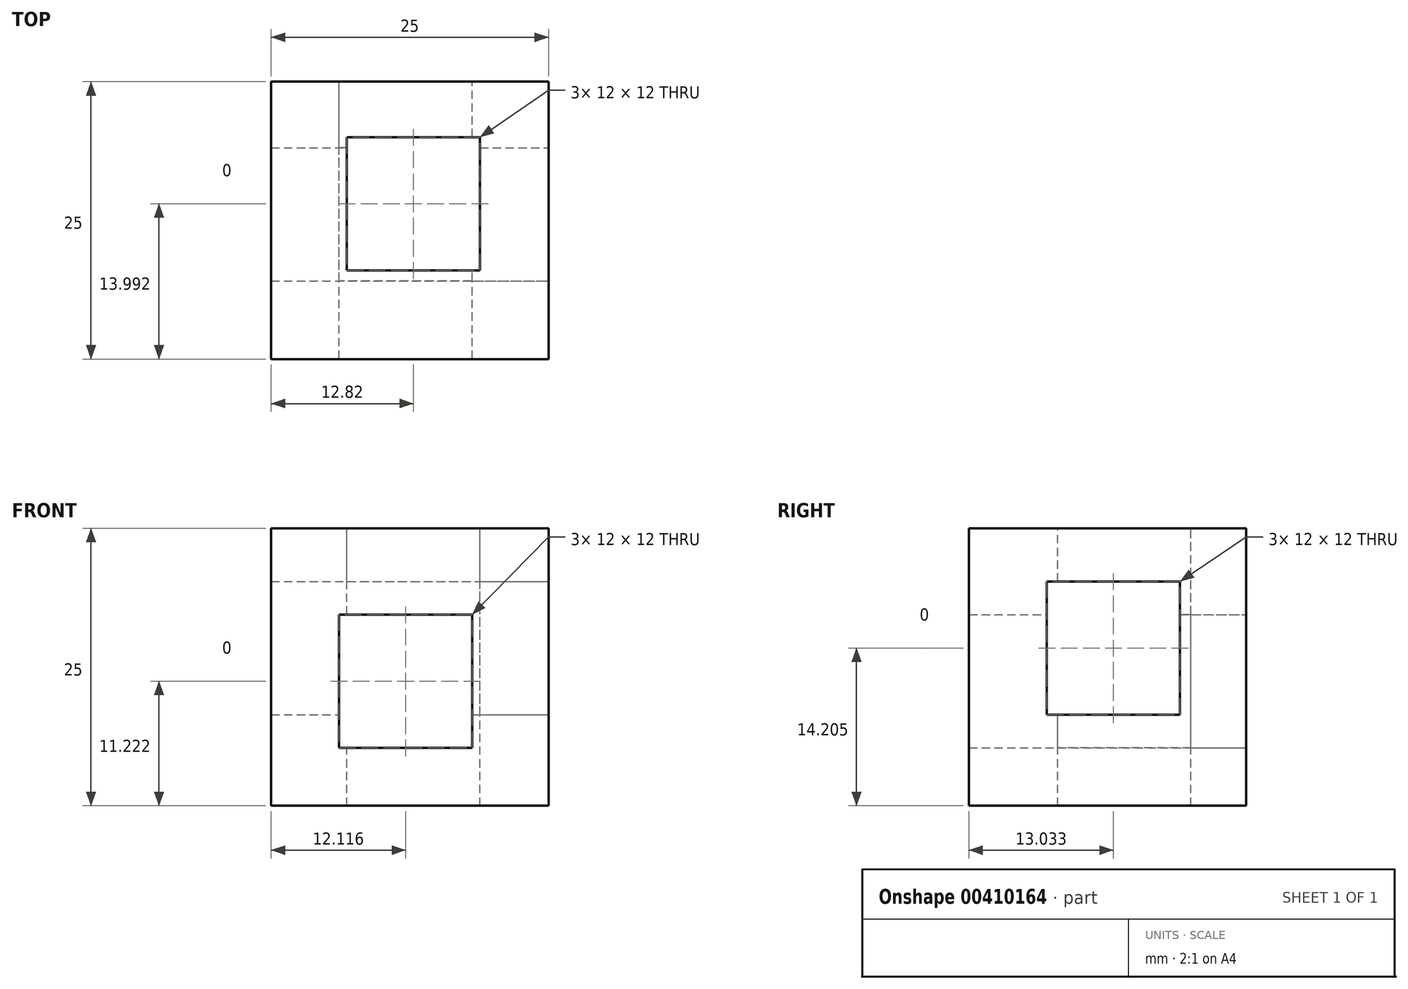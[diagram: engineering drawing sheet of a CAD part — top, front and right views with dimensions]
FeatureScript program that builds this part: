
annotation { "Feature Type Name" : "Feature", "Feature Type Description" : "" }
export const myFeature = defineFeature(function(context is Context, id is Id, definition is map)
    precondition{}
    {
        {
            var Q0;
            Q0=qCreatedBy(makeId("Top.planeOp"),FACE);
            var sketch = newSketch(context, id + "F0", { "sketchPlane" : qUnion([Q0])});
            skLineSegment(sketch, "E0.bottom", {"start": v(0, 0) * mm, "end": v(25, 0) * mm});
            skLineSegment(sketch, "E0.top", {"start": v(0, 25) * mm, "end": v(25, 25) * mm});
            skLineSegment(sketch, "E0.left", {"start": v(0, 0) * mm, "end": v(0, 25) * mm});
            skLineSegment(sketch, "E0.right", {"start": v(25, 0) * mm, "end": v(25, 25) * mm});
            skSolve(sketch);
        }
        {
            var Q0;
            Q0=makeQuery(id+"F0.imprint","IMPRINT",FACE,{"disambiguationData":[TD([[makeQuery(id+"F0.imprint","IMPRINT",EDGE,{"derivedFrom":sQuery(id+"F0.wireOp",EDGE,"E0.bottom")}),1.0]])]});
            extrude(context, id + "F1", {"entities" : qUnion([Q0]), "depth" : 25 * mm});
        }
        {
            var Q0;
            Q0=makeQuery(id+"F1.opExtrude","CAP_FACE",FACE,{"disambiguationData":[OSD([sQuery(id+"F0.wireOp",EDGE,"E0.bottom"),sQuery(id+"F0.wireOp",EDGE,"E0.top"),sQuery(id+"F0.wireOp",EDGE,"E0.left"),sQuery(id+"F0.wireOp",EDGE,"E0.right")])],"isStart":false});
            var sketch = newSketch(context, id + "F2", { "sketchPlane" : qUnion([Q0])});
            skLineSegment(sketch, "E1.bottom", {"start": v(6.82, 8) * mm, "end": v(18.82, 8) * mm});
            skLineSegment(sketch, "E1.top", {"start": v(6.82, 20) * mm, "end": v(18.82, 20) * mm});
            skLineSegment(sketch, "E1.left", {"start": v(6.82, 8) * mm, "end": v(6.82, 20) * mm});
            skLineSegment(sketch, "E1.right", {"start": v(18.82, 8) * mm, "end": v(18.82, 20) * mm});
            skSolve(sketch);
        }
        {
            var Q0;
            Q0=makeQuery(id+"F2.imprint","IMPRINT",FACE,{"disambiguationData":[TD([[makeQuery(id+"F2.imprint","IMPRINT",EDGE,{"derivedFrom":sQuery(id+"F2.wireOp",EDGE,"E1.bottom")}),1.0]])]});
            extrude(context, id + "F3", {"entities" : qUnion([Q0]), "operationType" : NewBodyOperationType.REMOVE, "oppositeDirection" : true, "depth" : 25 * mm});
        }
        {
            var Q0;
            Q0=makeQuery(id+"F1.opExtrude","SWEPT_FACE",FACE,{"disambiguationData":[OSD([sQuery(id+"F0.wireOp",EDGE,"E0.top")])]});
            var sketch = newSketch(context, id + "F4", { "sketchPlane" : qUnion([Q0])});
            skLineSegment(sketch, "E2.bottom", {"start": v(-6.12, 17.22) * mm, "end": v(-18.12, 17.22) * mm});
            skLineSegment(sketch, "E2.top", {"start": v(-6.12, 5.22) * mm, "end": v(-18.12, 5.22) * mm});
            skLineSegment(sketch, "E2.left", {"start": v(-6.12, 17.22) * mm, "end": v(-6.12, 5.22) * mm});
            skLineSegment(sketch, "E2.right", {"start": v(-18.12, 17.22) * mm, "end": v(-18.12, 5.22) * mm});
            skSolve(sketch);
        }
        {
            var Q0;
            Q0=makeQuery(id+"F4.imprint","IMPRINT",FACE,{"disambiguationData":[TD([[makeQuery(id+"F4.imprint","IMPRINT",EDGE,{"derivedFrom":sQuery(id+"F4.wireOp",EDGE,"E2.bottom")}),1.0]])]});
            extrude(context, id + "F5", {"entities" : qUnion([Q0]), "operationType" : NewBodyOperationType.REMOVE, "oppositeDirection" : true, "depth" : 25 * mm});
        }
        {
            var Q0;
            Q0=makeQuery(id+"F1.opExtrude","SWEPT_FACE",FACE,{"disambiguationData":[OSD([sQuery(id+"F0.wireOp",EDGE,"E0.right")])]});
            var sketch = newSketch(context, id + "F6", { "sketchPlane" : qUnion([Q0])});
            skLineSegment(sketch, "E3.bottom", {"start": v(7.03, 8.2) * mm, "end": v(19.03, 8.2) * mm});
            skLineSegment(sketch, "E3.top", {"start": v(7.03, 20.2) * mm, "end": v(19.03, 20.2) * mm});
            skLineSegment(sketch, "E3.left", {"start": v(7.03, 8.2) * mm, "end": v(7.03, 20.2) * mm});
            skLineSegment(sketch, "E3.right", {"start": v(19.03, 8.2) * mm, "end": v(19.03, 20.2) * mm});
            skSolve(sketch);
        }
        {
            var Q0;
            Q0=makeQuery(id+"F6.imprint","IMPRINT",FACE,{"disambiguationData":[TD([[makeQuery(id+"F6.imprint","IMPRINT",EDGE,{"derivedFrom":sQuery(id+"F6.wireOp",EDGE,"E3.bottom")}),1.0]])]});
            extrude(context, id + "F7", {"entities" : qUnion([Q0]), "operationType" : NewBodyOperationType.REMOVE, "oppositeDirection" : true, "depth" : 25 * mm});
        }
    });
